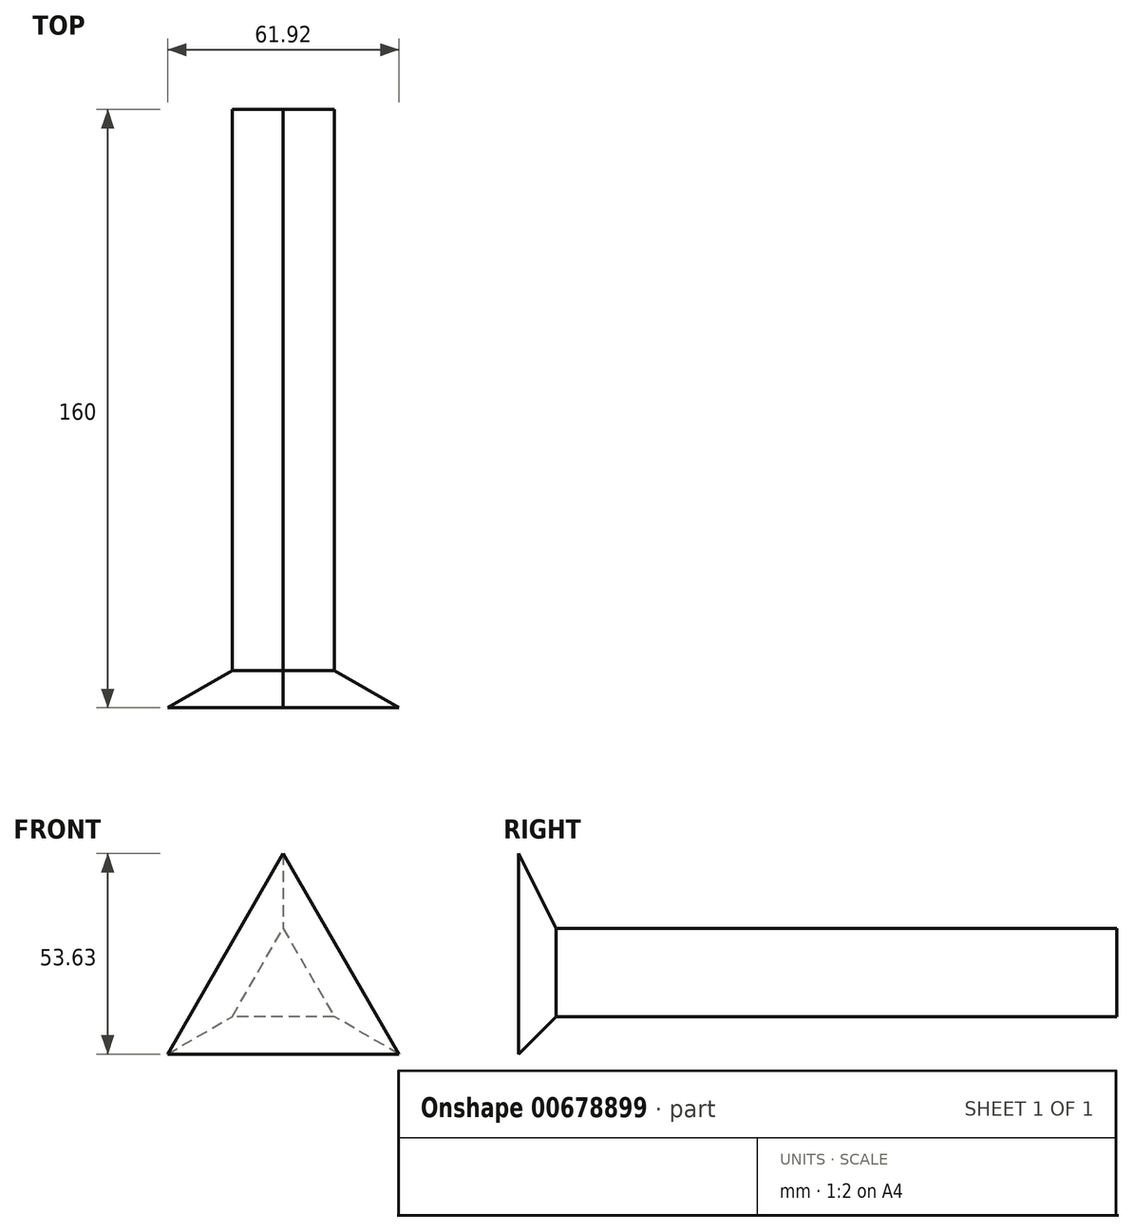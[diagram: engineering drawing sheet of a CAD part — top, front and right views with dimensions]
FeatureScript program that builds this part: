
annotation { "Feature Type Name" : "Feature", "Feature Type Description" : "" }
export const myFeature = defineFeature(function(context is Context, id is Id, definition is map)
    precondition{}
    {
        {
            var Q0;
            Q0=qCreatedBy(makeId("Front.planeOp"),FACE);
            var sketch = newSketch(context, id + "F0", { "sketchPlane" : qUnion([Q0])});
            skLineSegment(sketch, "E0.0", {"start": v(0, 15.75) * mm, "end": v(13.64, -7.88) * mm});
            skLineSegment(sketch, "E0.1", {"start": v(13.64, -7.88) * mm, "end": v(-13.64, -7.88) * mm});
            skLineSegment(sketch, "E0.2", {"start": v(-13.64, -7.88) * mm, "end": v(0, 15.75) * mm});
            skSolve(sketch);
        }
        {
            var Q0;
            Q0=makeQuery(id+"F0.imprint","IMPRINT",FACE,{"disambiguationData":[TD([[makeQuery(id+"F0.imprint","IMPRINT",EDGE,{"derivedFrom":sQuery(id+"F0.wireOp",EDGE,"E0.0")}),-1.0]])]});
            var Q1;
            Q1=sQuery(id+"F0.wireOp",EDGE,"E0.0");
            var Q2;
            Q2=sQuery(id+"F0.wireOp",EDGE,"E0.1");
            var Q3;
            Q3=sQuery(id+"F0.wireOp",EDGE,"E0.2");
            extrude(context, id + "F1", {"entities" : qUnion([Q0]), "surfaceEntities" : qUnion([Q1, Q2, Q3]), "depth" : 150 * mm, "offsetDistance" : 25 * mm});
        }
        {
            var Q0;
            Q0=makeQuery(id+"F1.opExtrude","CAP_FACE",FACE,{"disambiguationData":[OSD([sQuery(id+"F0.wireOp",EDGE,"E0.0"),sQuery(id+"F0.wireOp",EDGE,"E0.1"),sQuery(id+"F0.wireOp",EDGE,"E0.2")])],"isStart":false});
            extrude(context, id + "F2", {"entities" : qUnion([Q0]), "depth" : 10 * mm, "offsetDistance" : 25 * mm, "hasDraft" : true, "draftAngle" : 45 * degree});
        }
    });
